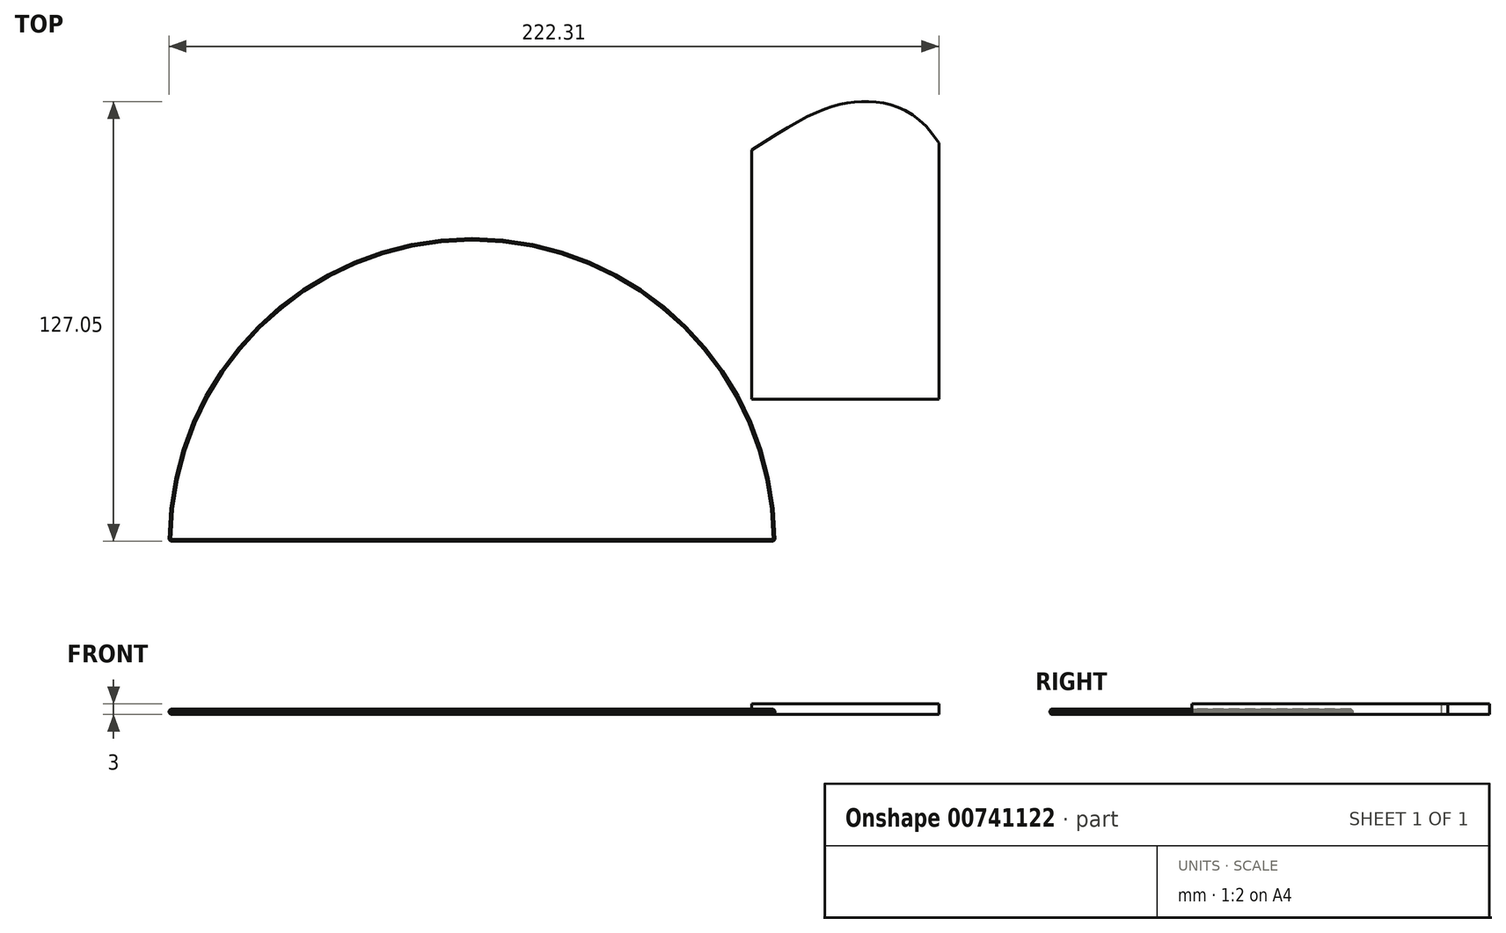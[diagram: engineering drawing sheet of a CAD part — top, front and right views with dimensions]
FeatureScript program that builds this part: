
annotation { "Feature Type Name" : "Feature", "Feature Type Description" : "" }
export const myFeature = defineFeature(function(context is Context, id is Id, definition is map)
    precondition{}
    {
        {
            var Q0;
            Q0=qCreatedBy(makeId("Top.planeOp"),FACE);
            var sketch = newSketch(context, id + "F0", { "sketchPlane" : qUnion([Q0])});
            skLineSegment(sketch, "E0", {"start": v(0, 0) * mm, "end": v(54, 0) * mm});
            skLineSegment(sketch, "E1", {"start": v(54, 0) * mm, "end": v(54, 74) * mm});
            skLineSegment(sketch, "E2", {"start": v(0, 0) * mm, "end": v(0, 72) * mm});
            skFitSpline(sketch, "E3", {"points": [v(54, 74) * mm, v(33, 86) * mm, v(0, 72) * mm], "startDerivative": vector(-39.97, 64.63) * mm, "endDerivative": vector(-89.31, -59.91) * mm});
            skSolve(sketch);
        }
        {
            var Q0;
            Q0=makeQuery(id+"F0.imprint","IMPRINT",FACE,{"disambiguationData":[TD([[makeQuery(id+"F0.imprint","IMPRINT",EDGE,{"derivedFrom":sQuery(id+"F0.wireOp",EDGE,"E0")}),1.0]])]});
            extrude(context, id + "F1", {"entities" : qUnion([Q0]), "depth" : 3 * mm, "offsetDistance" : 25 * mm});
        }
        {
            var Q0;
            Q0=qCreatedBy(makeId("Top.planeOp"),FACE);
            var sketch = newSketch(context, id + "F2", { "sketchPlane" : qUnion([Q0])});
            skLineSegment(sketch, "E4", {"start": v(-168.3, -41.05) * mm, "end": v(6.7, -41.05) * mm});
            skArc(sketch, "E5", {"start": v(6.7, -41.05) * mm, "mid": v(-80.8, 46.45) * mm, "end": v(-168.3, -41.05) * mm});
            skSolve(sketch);
        }
        {
            var Q0;
            Q0=makeQuery(id+"F2.imprint","IMPRINT",FACE,{"disambiguationData":[TD([[makeQuery(id+"F2.imprint","IMPRINT",EDGE,{"derivedFrom":sQuery(id+"F2.wireOp",EDGE,"E4")}),1.0]])]});
            extrude(context, id + "F3", {"entities" : qUnion([Q0]), "depth" : 1.5 * mm, "offsetDistance" : 25 * mm});
        }
        {
            var Q0;
            Q0=makeQuery(id+"F3.opExtrude","CAP_FACE",FACE,{"disambiguationData":[OSD([sQuery(id+"F2.wireOp",EDGE,"E4"),sQuery(id+"F2.wireOp",EDGE,"E5")])],"isStart":false});
            var Q1;
            Q1=makeQuery(id+"F3.opExtrude","CAP_FACE",FACE,{"disambiguationData":[OSD([sQuery(id+"F2.wireOp",EDGE,"E4"),sQuery(id+"F2.wireOp",EDGE,"E5")])],"isStart":true});
            var Q2;
            {var subQ0=sQuery(id+"F2.wireOp",EDGE,"E5");var subQ1=sQuery(id+"F2.wireOp",EDGE,"E4");Q2=makeQuery(id+"F3.opExtrude","SWEPT_EDGE",EDGE,{"disambiguationData":[OSD([subQ1,subQ0]),TDD([makeQuery(id+"F2.imprint","INTERSECT",VERTEX,{"disambiguationData":[OD(1.0)],"derivedFrom":[subQ1,subQ0]})])]});}
            var Q3;
            {var subQ0=sQuery(id+"F2.wireOp",EDGE,"E5");var subQ1=sQuery(id+"F2.wireOp",EDGE,"E4");Q3=makeQuery(id+"F3.opExtrude","SWEPT_EDGE",EDGE,{"disambiguationData":[OSD([subQ1,subQ0]),TDD([makeQuery(id+"F2.imprint","INTERSECT",VERTEX,{"disambiguationData":[OD(0.0)],"derivedFrom":[subQ1,subQ0]})])]});}
            chamfer(context, id + "F4", {"entities" : qUnion([Q0, Q1, Q2, Q3]), "width" : 0.5 * mm, "tangentPropagation" : true});
        }
    });
